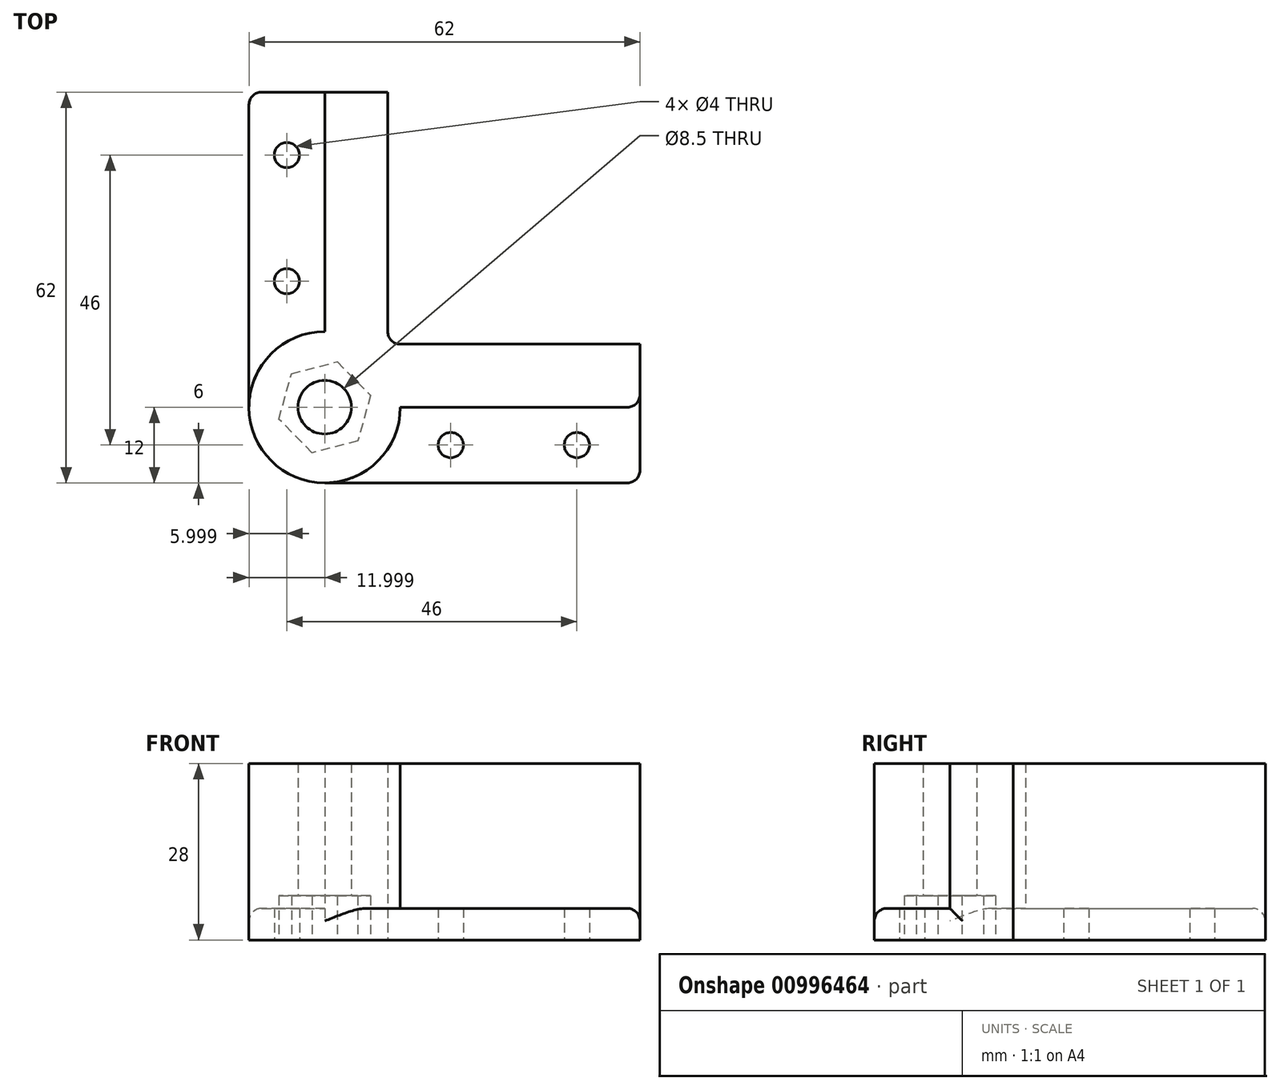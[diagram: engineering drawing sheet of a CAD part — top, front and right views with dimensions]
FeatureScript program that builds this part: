
annotation { "Feature Type Name" : "Feature", "Feature Type Description" : "" }
export const myFeature = defineFeature(function(context is Context, id is Id, definition is map)
    precondition{}
    {
        {
            var Q0;
            Q0=qCreatedBy(makeId("Top.planeOp"),FACE);
            var sketch = newSketch(context, id + "F0", { "sketchPlane" : qUnion([Q0])});
            skLineSegment(sketch, "E0", {"start": v(-3.05, 0) * mm, "end": v(36.95, 0) * mm});
            skLineSegment(sketch, "E1", {"start": v(36.95, 0) * mm, "end": v(36.95, -10) * mm});
            skLineSegment(sketch, "E2", {"start": v(36.95, -10) * mm, "end": v(-1.05, -10) * mm});
            skLineSegment(sketch, "E3", {"start": v(-13.05, 2) * mm, "end": v(-13.05, 40) * mm});
            skLineSegment(sketch, "E4", {"start": v(-13.05, 40) * mm, "end": v(-3.05, 40) * mm});
            skLineSegment(sketch, "E5", {"start": v(-3.05, 40) * mm, "end": v(-3.05, 0) * mm});
            skArc(sketch, "E6", {"start": v(-13.05, 2) * mm, "mid": v(-21.54, -18.49) * mm, "end": v(-1.05, -10) * mm});
            skLineSegment(sketch, "E7", {"start": v(-25.05, -10) * mm, "end": v(-25.05, 40) * mm});
            skLineSegment(sketch, "E8", {"start": v(-25.05, 40) * mm, "end": v(-13.05, 40) * mm});
            skLineSegment(sketch, "E9", {"start": v(36.95, -10) * mm, "end": v(36.95, -10) * mm});
            skLineSegment(sketch, "E10", {"start": v(-13.05, -22) * mm, "end": v(36.95, -22) * mm});
            skLineSegment(sketch, "E11", {"start": v(36.95, -22) * mm, "end": v(36.95, -10) * mm});
            skLineSegment(sketch, "E12", {"start": v(-1.05, -10) * mm, "end": v(-1.05, -10) * mm});
            skCircle(sketch, "E13", {"center": v(-19.05, 30) * mm, "radius": 2 * mm});
            skCircle(sketch, "E14", {"center": v(-19.05, 10) * mm, "radius": 2 * mm});
            skCircle(sketch, "E15", {"center": v(26.95, -16) * mm, "radius": 2 * mm});
            skCircle(sketch, "E16", {"center": v(6.95, -16) * mm, "radius": 2 * mm});
            skCircle(sketch, "E17", {"center": v(-13.05, -10) * mm, "radius": 4.25 * mm});
            skCircle(sketch, "E18.cCircle", {"center": v(-13.05, -10) * mm, "radius": 7.5 * mm, "construction": true});
            skLineSegment(sketch, "E18.0", {"start": v(-7.78, -15.34) * mm, "end": v(-15.04, -17.23) * mm});
            skLineSegment(sketch, "E18.1", {"start": v(-15.04, -17.23) * mm, "end": v(-20.3, -11.9) * mm});
            skLineSegment(sketch, "E18.2", {"start": v(-20.3, -11.9) * mm, "end": v(-18.32, -4.66) * mm});
            skLineSegment(sketch, "E18.3", {"start": v(-18.32, -4.66) * mm, "end": v(-11.06, -2.77) * mm});
            skLineSegment(sketch, "E18.4", {"start": v(-11.06, -2.77) * mm, "end": v(-5.8, -8.1) * mm});
            skLineSegment(sketch, "E18.5", {"start": v(-5.8, -8.1) * mm, "end": v(-7.78, -15.34) * mm});
            skSolve(sketch);
        }
        {
            var Q0;
            Q0=makeQuery(id+"F0.imprint","IMPRINT",FACE,{"disambiguationData":[TD([[makeQuery(id+"F0.imprint","IMPRINT",EDGE,{"derivedFrom":sQuery(id+"F0.wireOp",EDGE,"E0")}),-1.0]])]});
            extrude(context, id + "F1", {"entities" : qUnion([Q0]), "depth" : 28 * mm, "offsetDistance" : 25 * mm});
        }
        {
            var Q0;
            {var subQ2=sQuery(id+"F0.wireOp",EDGE,"E3");Q0=makeQuery(id+"F0.imprint","IMPRINT",FACE,{"disambiguationData":[TD([[makeQuery(id+"F0.imprint","IMPRINT",EDGE,{"derivedFrom":subQ2}),1.0]])]});}
            extrude(context, id + "F2", {"entities" : qUnion([Q0]), "operationType" : NewBodyOperationType.ADD, "depth" : 5 * mm, "offsetDistance" : 25 * mm});
        }
        {
            var Q0;
            {var subQ2=sQuery(id+"F0.wireOp",EDGE,"E2");Q0=makeQuery(id+"F0.imprint","IMPRINT",FACE,{"disambiguationData":[TD([[makeQuery(id+"F0.imprint","IMPRINT",EDGE,{"derivedFrom":subQ2}),1.0]])]});}
            extrude(context, id + "F3", {"entities" : qUnion([Q0]), "operationType" : NewBodyOperationType.ADD, "depth" : 5 * mm, "offsetDistance" : 25 * mm});
        }
        {
            var Q0;
            Q0=makeQuery(id+"F0.imprint","IMPRINT",FACE,{"disambiguationData":[TD([[makeQuery(id+"F0.imprint","IMPRINT",EDGE,{"derivedFrom":sQuery(id+"F0.wireOp",EDGE,"E17")}),-1.0]])]});
            extrude(context, id + "F4", {"entities" : qUnion([Q0]), "operationType" : NewBodyOperationType.ADD, "depth" : 28 * mm, "offsetDistance" : 25 * mm});
        }
        {
            var Q0;
            Q0=makeQuery(id+"F0.imprint","IMPRINT",FACE,{"disambiguationData":[TD([[makeQuery(id+"F0.imprint","IMPRINT",EDGE,{"derivedFrom":sQuery(id+"F0.wireOp",EDGE,"E17")}),-1.0]])]});
            extrude(context, id + "F5", {"entities" : qUnion([Q0]), "operationType" : NewBodyOperationType.REMOVE, "depth" : 7 * mm, "offsetDistance" : 25 * mm});
        }
        {
            var Q0;
            Q0=makeQuery(id+"F1.opExtrude","SWEPT_EDGE",EDGE,{"disambiguationData":[OSD([sQuery(id+"F0.wireOp",EDGE,"E1"),sQuery(id+"F0.wireOp",EDGE,"E2"),sQuery(id+"F0.wireOp",EDGE,"E11")])]});
            var Q1;
            Q1=makeQuery(id+"F3.opExtrude","CAP_EDGE",EDGE,{"disambiguationData":[OSD([sQuery(id+"F0.wireOp",EDGE,"E11")])],"isStart":false});
            var Q2;
            Q2=makeQuery(id+"F2.opExtrude","CAP_EDGE",EDGE,{"disambiguationData":[OSD([sQuery(id+"F0.wireOp",EDGE,"E8")])],"isStart":false});
            var Q3;
            Q3=makeQuery(id+"F3.opExtrude","SWEPT_EDGE",EDGE,{"disambiguationData":[OSD([sQuery(id+"F0.wireOp",EDGE,"E10"),sQuery(id+"F0.wireOp",EDGE,"E11")])]});
            var Q4;
            Q4=makeQuery(id+"F2.opExtrude","SWEPT_EDGE",EDGE,{"disambiguationData":[OSD([sQuery(id+"F0.wireOp",EDGE,"E7"),sQuery(id+"F0.wireOp",EDGE,"E8")])]});
            var Q5;
            Q5=makeQuery(id+"F1.opExtrude","SWEPT_EDGE",EDGE,{"disambiguationData":[OSD([sQuery(id+"F0.wireOp",EDGE,"E0"),sQuery(id+"F0.wireOp",EDGE,"E5")])]});
            var Q6;
            Q6=makeQuery(id+"F3.opExtrude","CAP_EDGE",EDGE,{"disambiguationData":[OSD([sQuery(id+"F0.wireOp",EDGE,"E10")])],"isStart":false});
            var Q7;
            Q7=makeQuery(id+"F2.opExtrude","CAP_EDGE",EDGE,{"disambiguationData":[OSD([sQuery(id+"F0.wireOp",EDGE,"E7")])],"isStart":false});
            var Q8;
            Q8=makeQuery(id+"F3.opExtrude","CAP_EDGE",EDGE,{"disambiguationData":[OSD([sQuery(id+"F0.wireOp",EDGE,"E2")])],"isStart":false});
            var Q9;
            Q9=makeQuery(id+"F2.opExtrude","CAP_EDGE",EDGE,{"disambiguationData":[OSD([sQuery(id+"F0.wireOp",EDGE,"E3")])],"isStart":false});
            fillet(context, id + "F6", {"entities" : qUnion([Q0, Q1, Q2, Q3, Q4, Q5, Q6, Q7, Q8, Q9]), "radius" : 2 * mm, "tangentPropagation" : true, "allowEdgeOverflow" : false});
        }
    });
